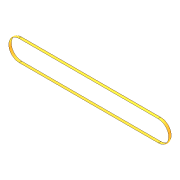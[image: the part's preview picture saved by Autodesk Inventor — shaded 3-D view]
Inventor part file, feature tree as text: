
AUTODESK INVENTOR PART (.ipt)
format: ipt  version: 2012 (Build 160160000, 160)  size: 84,480 bytes
history: native  units: in
note: dims shown in document units (in); Inventor stores cm internally (conversion verified against a paired STEP export)
features: extrude x1, fillet x1, sketch x1
ambient origin geometry x8: Origin, YZ Plane, XZ Plane, XY Plane, X Axis, Y Axis, Z Axis, Center Point
bodies: Solid1 (feature_tree)
feature tree (3):
  extrude  "Extrusion1"  Depth=10.0in
  fillet  "Fillet1"  Radius=0.1875in
  sketch  "Sketch1"  dims[d0=0.75in d1=10.0in d2=0.1875in d3=0.1875in d4=0.0in d5=0.125in]
